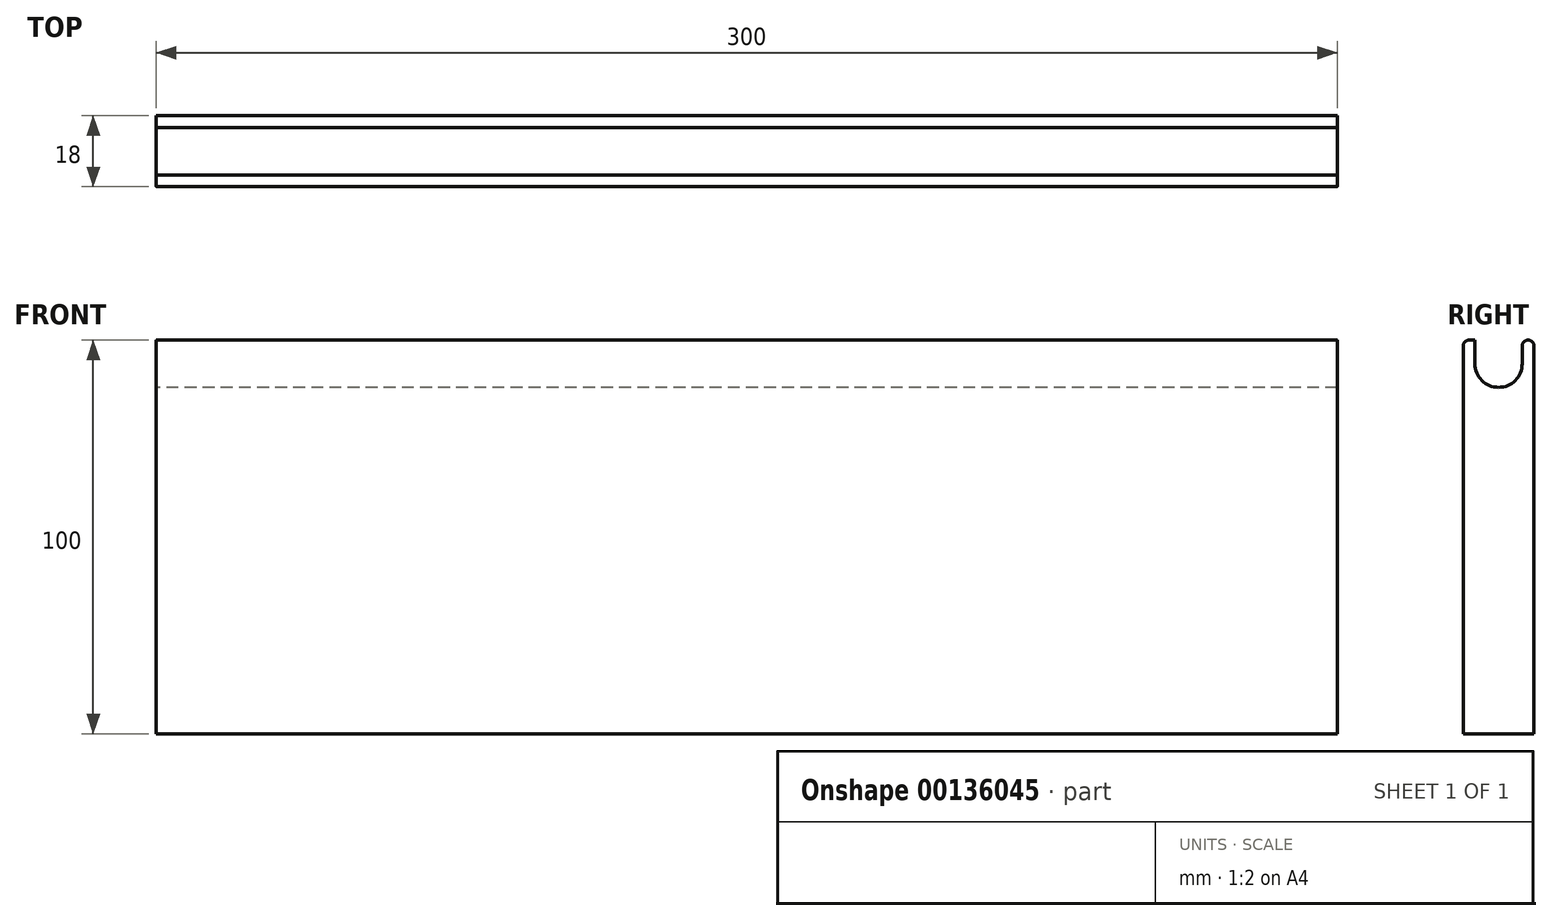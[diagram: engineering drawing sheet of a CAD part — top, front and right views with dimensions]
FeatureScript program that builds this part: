
annotation { "Feature Type Name" : "Feature", "Feature Type Description" : "" }
export const myFeature = defineFeature(function(context is Context, id is Id, definition is map)
    precondition{}
    {
        {
            var Q0;
            Q0=qCreatedBy(makeId("Front.planeOp"),FACE);
            var sketch = newSketch(context, id + "F0", { "sketchPlane" : qUnion([Q0])});
            skLineSegment(sketch, "E0.bottom", {"start": v(-153.72, -55.78) * mm, "end": v(146.28, -55.78) * mm});
            skLineSegment(sketch, "E0.top", {"start": v(-153.72, -155.78) * mm, "end": v(146.28, -155.78) * mm});
            skLineSegment(sketch, "E0.left", {"start": v(-153.72, -55.78) * mm, "end": v(-153.72, -155.78) * mm});
            skLineSegment(sketch, "E0.right", {"start": v(146.28, -55.78) * mm, "end": v(146.28, -155.78) * mm});
            skSolve(sketch);
        }
        {
            var Q0;
            Q0=makeQuery(id+"F0.imprint","IMPRINT",FACE,{"disambiguationData":[TD([[makeQuery(id+"F0.imprint","IMPRINT",EDGE,{"derivedFrom":sQuery(id+"F0.wireOp",EDGE,"E0.bottom")}),-1.0]])]});
            extrude(context, id + "F1", {"entities" : qUnion([Q0]), "endBound" : BoundingType.SYMMETRIC, "depth" : 18 * mm});
        }
        {
            var Q0;
            Q0=makeQuery(id+"F1.opExtrude","SWEPT_FACE",FACE,{"disambiguationData":[OSD([sQuery(id+"F0.wireOp",EDGE,"E0.right")])]});
            var sketch = newSketch(context, id + "F2", { "sketchPlane" : qUnion([Q0])});
            skLineSegment(sketch, "E1", {"start": v(6, -55.78) * mm, "end": v(6, -67.78) * mm});
            skLineSegment(sketch, "E2", {"start": v(6, -67.78) * mm, "end": v(-6, -67.78) * mm});
            skLineSegment(sketch, "E3", {"start": v(-6, -67.78) * mm, "end": v(-6, -55.78) * mm});
            skLineSegment(sketch, "E4", {"start": v(-6, -55.78) * mm, "end": v(6, -55.78) * mm});
            skSolve(sketch);
        }
        {
            var Q0;
            Q0=makeQuery(id+"F2.imprint","IMPRINT",FACE,{"disambiguationData":[TD([[makeQuery(id+"F2.imprint","IMPRINT",EDGE,{"derivedFrom":sQuery(id+"F2.wireOp",EDGE,"E1")}),-1.0]])]});
            extrude(context, id + "F3", {"entities" : qUnion([Q0]), "operationType" : NewBodyOperationType.REMOVE, "endBound" : BoundingType.THROUGH_ALL, "oppositeDirection" : true, "depth" : 25 * mm});
        }
        {
            var Q0;
            Q0=makeQuery(id+"F3.boolean.opBoolean","COPY",EDGE,{"derivedFrom":makeQuery(id+"F3.opExtrude","SWEPT_EDGE",EDGE,{"disambiguationData":[OSD([sQuery(id+"F2.wireOp",EDGE,"E1"),sQuery(id+"F2.wireOp",EDGE,"E2")])]})});
            var Q1;
            Q1=makeQuery(id+"F3.boolean.opBoolean","COPY",EDGE,{"derivedFrom":makeQuery(id+"F3.opExtrude","SWEPT_EDGE",EDGE,{"disambiguationData":[OSD([sQuery(id+"F2.wireOp",EDGE,"E2"),sQuery(id+"F2.wireOp",EDGE,"E3")])]})});
            fillet(context, id + "F4", {"entities" : qUnion([Q0, Q1]), "radius" : 6 * mm, "tangentPropagation" : true, "allowEdgeOverflow" : false});
        }
        {
            var Q0;
            Q0=makeQuery(id+"F1.opExtrude","CAP_EDGE",EDGE,{"disambiguationData":[OSD([sQuery(id+"F0.wireOp",EDGE,"E0.bottom")])],"isStart":false});
            var Q1;
            Q1=makeQuery(id+"F3.boolean.opBoolean","COPY",EDGE,{"derivedFrom":makeQuery(id+"F3.opExtrude","SWEPT_EDGE",EDGE,{"disambiguationData":[OSD([sQuery(id+"F0.wireOp",EDGE,"E0.bottom"),sQuery(id+"F0.wireOp",EDGE,"E0.right"),sQuery(id+"F2.wireOp",EDGE,"E3"),sQuery(id+"F2.wireOp",EDGE,"E4")])]})});
            var Q2;
            Q2=makeQuery(id+"F3.boolean.opBoolean","COPY",EDGE,{"derivedFrom":makeQuery(id+"F3.opExtrude","SWEPT_EDGE",EDGE,{"disambiguationData":[OSD([sQuery(id+"F0.wireOp",EDGE,"E0.bottom"),sQuery(id+"F0.wireOp",EDGE,"E0.right"),sQuery(id+"F2.wireOp",EDGE,"E1"),sQuery(id+"F2.wireOp",EDGE,"E4")])]})});
            var Q3;
            Q3=makeQuery(id+"F1.opExtrude","CAP_EDGE",EDGE,{"disambiguationData":[OSD([sQuery(id+"F0.wireOp",EDGE,"E0.bottom")])],"isStart":true});
            fillet(context, id + "F5", {"entities" : qUnion([Q0, Q1, Q2, Q3]), "radius" : 1.5 * mm, "tangentPropagation" : true, "allowEdgeOverflow" : false});
        }
    });
